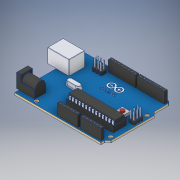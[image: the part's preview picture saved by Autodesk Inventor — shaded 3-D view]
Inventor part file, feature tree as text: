
AUTODESK INVENTOR PART (.ipt)
format: ipt  version: 2019 (Build 230136000, 136)  size: 2,386,944 bytes
history: mixed  units: mm
features: extrude x2, other x1, sketch x1, imported_body x1
ambient origin geometry x8: Origin, YZ Plane, XZ Plane, XY Plane, X Axis, Y Axis, Z Axis, Center Point
bodies: Body1 (imported_parasolid)
feature tree (5):
  other  "Твердое тело1"
  extrude  "Выдавливание1"  TaperAngle=0.0deg  [1 undecoded]
  sketch  "Эскиз1"
  extrude  "Extrude19"  [1 undecoded]
  imported_body  NMx_Import_Brep_tag  [imported B-rep: ~53 faces, bbox_mm=[66.973089, 9.9695, 53.34]]
note: 2 required parameter values undecoded (feature->parameter linkage not recoverable at this tier; creation-order binding heuristic only, values carry confidence <= 0.55)
